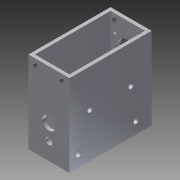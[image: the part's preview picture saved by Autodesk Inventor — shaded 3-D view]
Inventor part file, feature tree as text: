
AUTODESK INVENTOR PART (.ipt)
format: ipt  version: 2013 (Build 170138000, 138)  size: 199,168 bytes
history: native  units: mm
features: sketch x7, hole x5, thread x4, extrude x2, other x1
ambient origin geometry x1: Origin
feature tree (19):
  other  "ソリッド1"
  extrude  "押し出し1"  Depth=25.0mm
  extrude  "押し出し2"  Depth=50.0mm
  hole  "穴1"  [1 undecoded]
  hole  "穴2"  [1 undecoded]
  hole  "穴4"  [1 undecoded]
  thread  "ねじ1"
  thread  "ねじ2"
  thread  "ねじ3"
  thread  "ねじ4"
  hole  "穴5"  [1 undecoded]
  hole  "穴7"  [1 undecoded]
  sketch  "スケッチ1"
  sketch  "スケッチ2"
  sketch  "スケッチ3"
  sketch  "スケッチ4"
  sketch  "スケッチ5"
  sketch  "スケッチ7"
  sketch  "スケッチ8"
note: 5 required parameter values undecoded (feature->parameter linkage not recoverable at this tier; creation-order binding heuristic only, values carry confidence <= 0.55)
